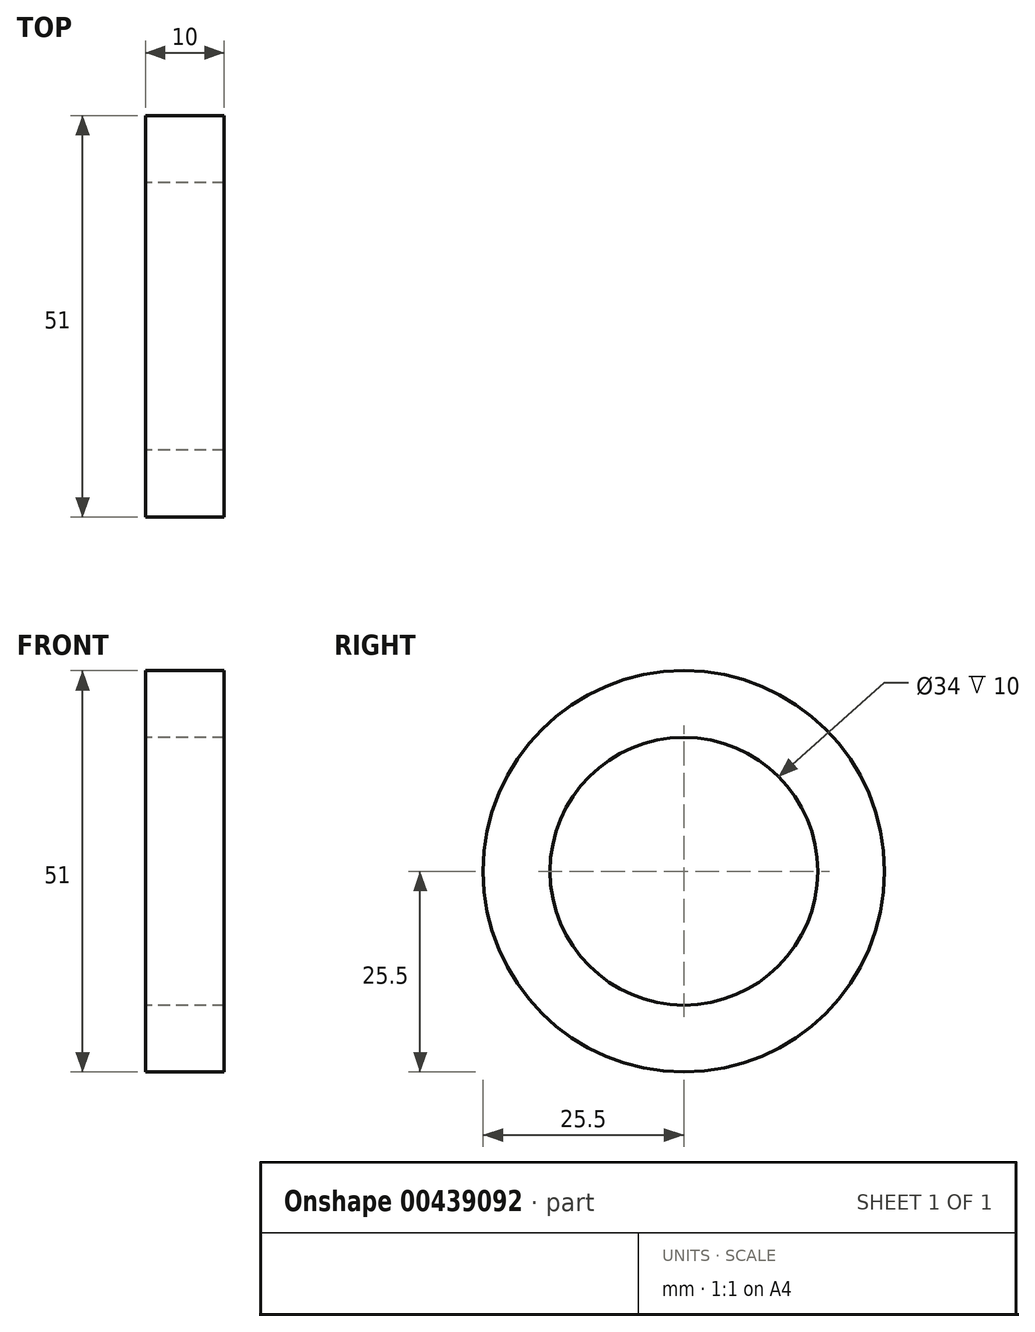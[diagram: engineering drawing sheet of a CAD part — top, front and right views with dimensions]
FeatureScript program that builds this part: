
annotation { "Feature Type Name" : "Feature", "Feature Type Description" : "" }
export const myFeature = defineFeature(function(context is Context, id is Id, definition is map)
    precondition{}
    {
        {
            var Q0;
            Q0=qCreatedBy(makeId("Right.planeOp"),FACE);
            var sketch = newSketch(context, id + "F0", { "sketchPlane" : qUnion([Q0])});
            skCircle(sketch, "E0", {"center": v(0, 0) * mm, "radius": 25.5 * mm});
            skCircle(sketch, "E1", {"center": v(0, 0) * mm, "radius": 17 * mm});
            skSolve(sketch);
        }
        {
            var Q0;
            Q0=qSketchRegion(id+"F0",true);
            extrude(context, id + "F1", {"entities" : qUnion([Q0]), "depth" : 10 * mm});
        }
    });
